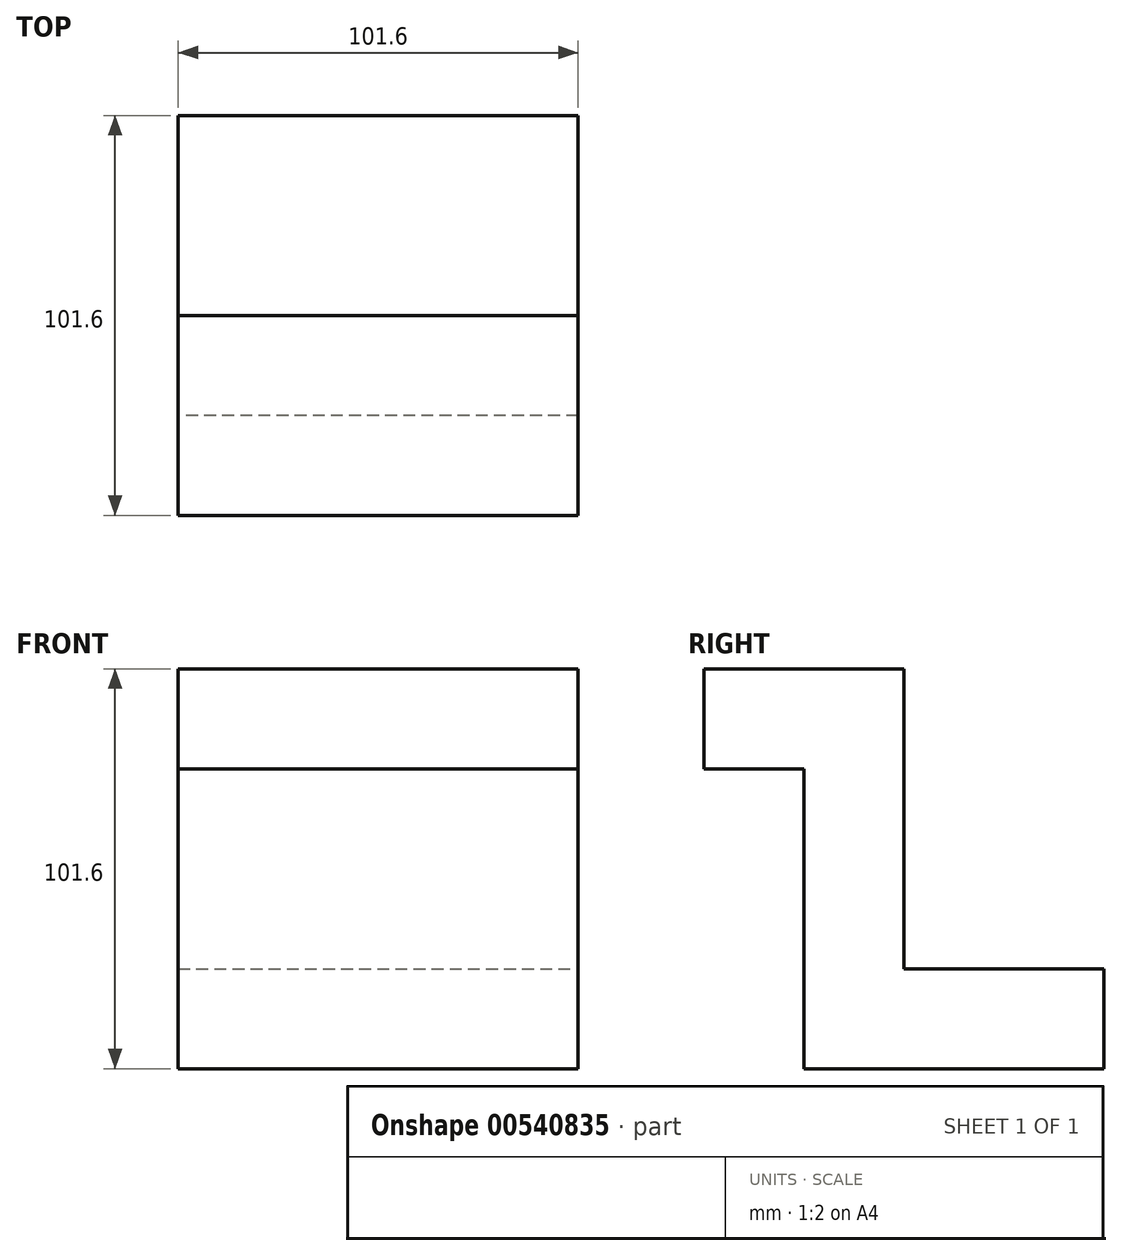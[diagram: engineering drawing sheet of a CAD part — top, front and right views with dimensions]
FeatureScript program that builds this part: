
annotation { "Feature Type Name" : "Feature", "Feature Type Description" : "" }
export const myFeature = defineFeature(function(context is Context, id is Id, definition is map)
    precondition{}
    {
        {
            var Q0;
            Q0=qCreatedBy(makeId("Front.planeOp"),FACE);
            var sketch = newSketch(context, id + "F0", { "sketchPlane" : qUnion([Q0])});
            skLineSegment(sketch, "E0", {"start": v(0, 0) * mm, "end": v(-101.6, 0) * mm});
            skLineSegment(sketch, "E1", {"start": v(-101.6, 0) * mm, "end": v(-101.6, 101.6) * mm});
            skLineSegment(sketch, "E2", {"start": v(-101.6, 101.6) * mm, "end": v(0, 101.6) * mm});
            skLineSegment(sketch, "E3", {"start": v(0, 101.6) * mm, "end": v(0, 0) * mm});
            skSolve(sketch);
        }
        {
            var Q0;
            Q0=makeQuery(id+"F0.imprint","IMPRINT",FACE,{"disambiguationData":[TD([[makeQuery(id+"F0.imprint","IMPRINT",EDGE,{"derivedFrom":sQuery(id+"F0.wireOp",EDGE,"E0")}),-1.0]])]});
            extrude(context, id + "F1", {"entities" : qUnion([Q0]), "depth" : 76.2 * mm, "offsetDistance" : 25.4 * mm});
        }
        {
            var Q0;
            Q0=makeQuery(id+"F1.opExtrude","SWEPT_FACE",FACE,{"disambiguationData":[OSD([sQuery(id+"F0.wireOp",EDGE,"E3")])]});
            var sketch = newSketch(context, id + "F2", { "sketchPlane" : qUnion([Q0])});
            skLineSegment(sketch, "E4", {"start": v(0, 0) * mm, "end": v(0, 25.4) * mm});
            skLineSegment(sketch, "E5", {"start": v(0, 25.4) * mm, "end": v(-50.8, 25.4) * mm});
            skLineSegment(sketch, "E6", {"start": v(-50.8, 25.4) * mm, "end": v(-50.8, 101.6) * mm});
            skLineSegment(sketch, "E7", {"start": v(-50.8, 101.6) * mm, "end": v(-76.2, 101.6) * mm});
            skSolve(sketch);
        }
        {
            var Q0;
            Q0=makeQuery(id+"F1.opExtrude","CAP_FACE",FACE,{"disambiguationData":[OSD([sQuery(id+"F0.wireOp",EDGE,"E0"),sQuery(id+"F0.wireOp",EDGE,"E1"),sQuery(id+"F0.wireOp",EDGE,"E2"),sQuery(id+"F0.wireOp",EDGE,"E3")])],"isStart":false});
            var sketch = newSketch(context, id + "F3", { "sketchPlane" : qUnion([Q0])});
            skLineSegment(sketch, "E8", {"start": v(0, 0) * mm, "end": v(0, 76.2) * mm});
            skLineSegment(sketch, "E9", {"start": v(0, 76.2) * mm, "end": v(-101.6, 76.2) * mm});
            skSolve(sketch);
        }
        {
            var Q0;
            Q0 = qSketchRegion(id + "F3", true);
            var Q1;
            {var subQ0=sQuery(id+"F3.wireOp",EDGE,"E9");Q1=makeQuery(id+"F3.imprint","IMPRINT",FACE,{"disambiguationData":[TD([[makeQuery(id+"F3.imprint","IMPRINT",EDGE,{"derivedFrom":subQ0}),-1.0]])]});}
            extrude(context, id + "F4", {"entities" : qUnion([Q0, Q1]), "operationType" : NewBodyOperationType.ADD, "depth" : 25.4 * mm, "offsetDistance" : 25.4 * mm});
        }
        {
            var Q0;
            {var subQ0=sQuery(id+"F2.wireOp",EDGE,"E5");Q0=makeQuery(id+"F2.imprint","IMPRINT",FACE,{"disambiguationData":[TD([[makeQuery(id+"F2.imprint","IMPRINT",EDGE,{"derivedFrom":subQ0}),-1.0]])]});}
            extrude(context, id + "F5", {"entities" : qUnion([Q0]), "operationType" : NewBodyOperationType.REMOVE, "oppositeDirection" : true, "depth" : 101.6 * mm, "offsetDistance" : 25.4 * mm});
        }
    });
